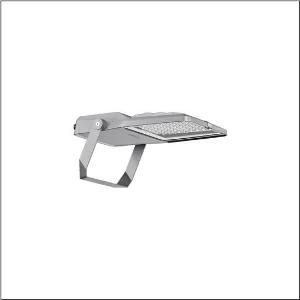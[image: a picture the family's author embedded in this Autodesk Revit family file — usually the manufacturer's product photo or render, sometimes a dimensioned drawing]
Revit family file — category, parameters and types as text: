
# Revit family: floodlight_fl_21_iq_mini___pl61_5xa7771b2c1a_d515
name_source: partatom
category: Lighting Fixtures
units: mm (PartAtom-declared; Revit-internal decimal feet)

## family parameters
Cut with Voids When Loaded = No
Host = Face
Light Source = No
Part Type = Normal
Room Calculation Point = No
Round Connector Dimension = Use Diameter
Shared = No

## types (1)
- --- (1 x LED, 6120 lm, 45.5 W, 3000K)
    Apparent Load = 46 VA
    CIE Flux Codes = 33 65 98 100 100
    Color Rendering = 70
    Color Temperature = 3000K
    Default Elevation = 1800 mm
    Description = Floodlight FL 21 iQ mini, floodlight, primary light control with lens, of PMMA, primary optical cover: protective disc, of toughened safety glass, transparent, light distribution: PL61, light emission: direct distribution, installation type: surface-mounted, LED, High Power LED, rated luminous flux: 6.120lm, luminous efficacy: 135lm/W, light colour: 730, colour temperature: 3000K, control: Auto-Match, Temp-Guard, Lumen-Switch, Night-Set, Smart-Wire, Light-Fading, Desk-Remote (wireless, voltage-free reading and setting of iQ features in the workshop via application-optimized NFC function/RFID function), optimised constant luminous flux control (CLO 2.0), with terminal, 6-pole, mains connection: 220..240V, AC, 50/60Hz, start of lifetime: 46W, end of service life: 48W, reduction: 22W, luminaire housing, of diecast aluminium, powder-coated, Siteco® metallic grey (DB 702S), corrosivity category C5 mid according to DIN EN ISO 12944, sealing non-destructively replaceable, mounting bracket, of steel, galvanised, powder-coated, Siteco® metallic grey (DB 702S), protection rating (complete): IP66, insulation class (complete): insulation class II (safety insulation), certification: CE, ENEC, VDE, protection symbol: D, impact resistance: IK08, permissible operating ambient temperature: -40..+40°C, permissible operating ambient temperature for outdoor applications: -40..+50°C, standard: DIN EN 12944, LABS conformity tested according to VDMA 24364:2018-05, packaging unit: 1 piece

Light Distribution: PL61
    Height = 70 mm
    Lamp = 1 x LED
    Lamp Light Flux = 6120 lm
    Lamp Power = 45.5 W
    Lamp count = 1
    Length = 485 mm
    Luminous efficacy = 135 lm/W
    Manufacturer = Siteco
    ModVariant = No
    Model = 5XA7771B2C1A
    Mounting Place = Wall
    Mounting Type = Surface mounted
    Number of Poles = 1
    OnlyDefault = Yes
    Power Factor = 1
    Product Name = Floodlight FL 21 iQ mini | PL61
    Product group = floodlight | wall mounted
    ProductGroupID = 2001
    Protection Class = Protection class II
    Protection Degree = IP 66
    RLX_Detail_Level = 1
    RLX_Emergency_Light_Flux = 0 lm
    RLX_Emergency_Type = 0
    RLX_Emergency_Type_DB = No
    RlxData = <blob elided: 96197 chars, md5=73129dff>
    Socket = socket
    Standby Power = 0 W
    System Light Flux = 6120 lm
    System Power = 46 W
    Type Comments = factory setting: luminous flux: 100 % | dim-lin: 254 | 463 mA
    Type Image = l_1006845.jpg
    URL = http://relux.com
    VarID = @adj_106983
    Voltage = 0 V
    Weight = 0.00 kg
    Width = 337 mm

## geometry (parser evidence)
native form markers: Blend x4, Sweep x12
no freeform markers — native parametric forms only
